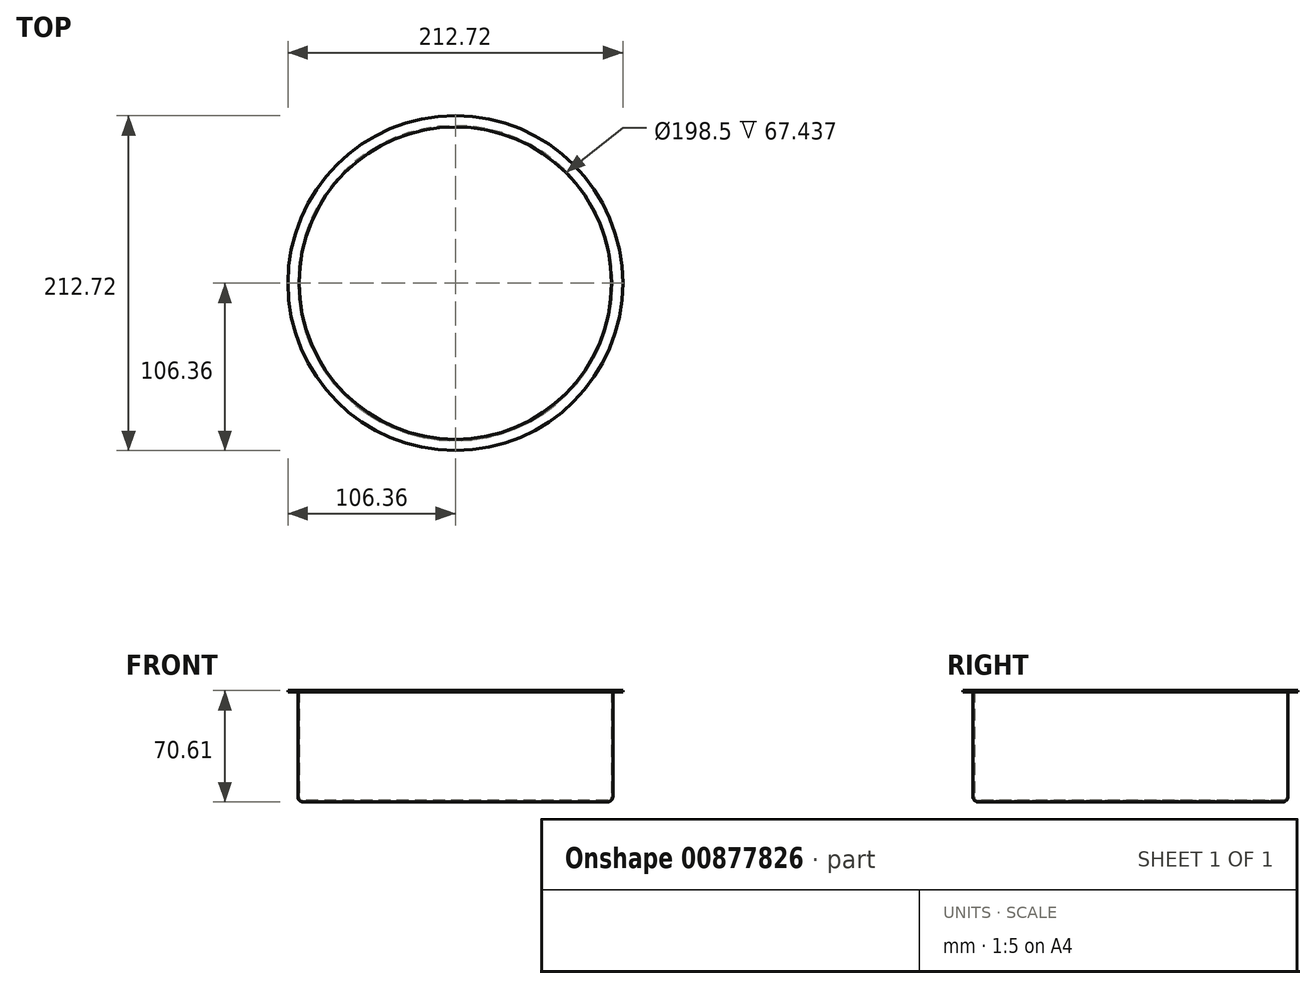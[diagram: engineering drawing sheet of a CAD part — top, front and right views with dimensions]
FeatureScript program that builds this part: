
annotation { "Feature Type Name" : "Feature", "Feature Type Description" : "" }
export const myFeature = defineFeature(function(context is Context, id is Id, definition is map)
    precondition{}
    {
        {
            var Q0;
            Q0=qCreatedBy(makeId("Front.planeOp"),FACE);
            var sketch = newSketch(context, id + "F0", { "sketchPlane" : qUnion([Q0])});
            skLineSegment(sketch, "E0", {"start": v(-106.36, 69.85) * mm, "end": v(-100.01, 69.85) * mm});
            skLineSegment(sketch, "E1", {"start": v(-100.01, 69.85) * mm, "end": v(-100.01, 0) * mm});
            skLineSegment(sketch, "E2", {"start": v(-100.01, 0) * mm, "end": v(0, 0) * mm});
            skLineSegment(sketch, "E3", {"start": v(0, 0) * mm, "end": v(0, 66.43) * mm, "construction": true});
            skLineSegment(sketch, "E4.0", {"start": v(-99.25, 0.76) * mm, "end": v(0, 0.76) * mm});
            skLineSegment(sketch, "E4.1", {"start": v(-99.25, 70.61) * mm, "end": v(-99.25, 0.76) * mm});
            skLineSegment(sketch, "E4.2", {"start": v(-106.36, 70.61) * mm, "end": v(-99.25, 70.61) * mm});
            skLineSegment(sketch, "E5", {"start": v(0, 0.76) * mm, "end": v(0, 0) * mm});
            skLineSegment(sketch, "E6", {"start": v(-106.36, 70.61) * mm, "end": v(-106.36, 69.85) * mm});
            skSolve(sketch);
        }
        {
            var Q0;
            Q0 = qSketchRegion(id + "F0", true);
            var Q1;
            Q1=sQuery(id+"F0.wireOp",EDGE,"E3");
            revolve(context, id + "F1", {"surfaceOperationType" : NewSurfaceOperationType.NEW, "entities" : qUnion([Q0]), "axis" : qUnion([Q1]), "revolveType" : RevolveType.FULL});
        }
        {
            var Q0;
            Q0=makeQuery(id+"F1.opRevolve","SWEPT_EDGE",EDGE,{"disambiguationData":[OSD([sQuery(id+"F0.wireOp",EDGE,"E4.0"),sQuery(id+"F0.wireOp",EDGE,"E4.1")])]});
            fillet(context, id + "F2", {"entities" : qUnion([Q0]), "radius" : 2.41 * mm, "tangentPropagation" : true, "allowEdgeOverflow" : false});
        }
        {
            var Q0;
            Q0=makeQuery(id+"F1.opRevolve","SWEPT_EDGE",EDGE,{"disambiguationData":[OSD([sQuery(id+"F0.wireOp",EDGE,"E1"),sQuery(id+"F0.wireOp",EDGE,"E2")])]});
            fillet(context, id + "F3", {"entities" : qUnion([Q0]), "radius" : 3.17 * mm, "allowEdgeOverflow" : false});
        }
    });
